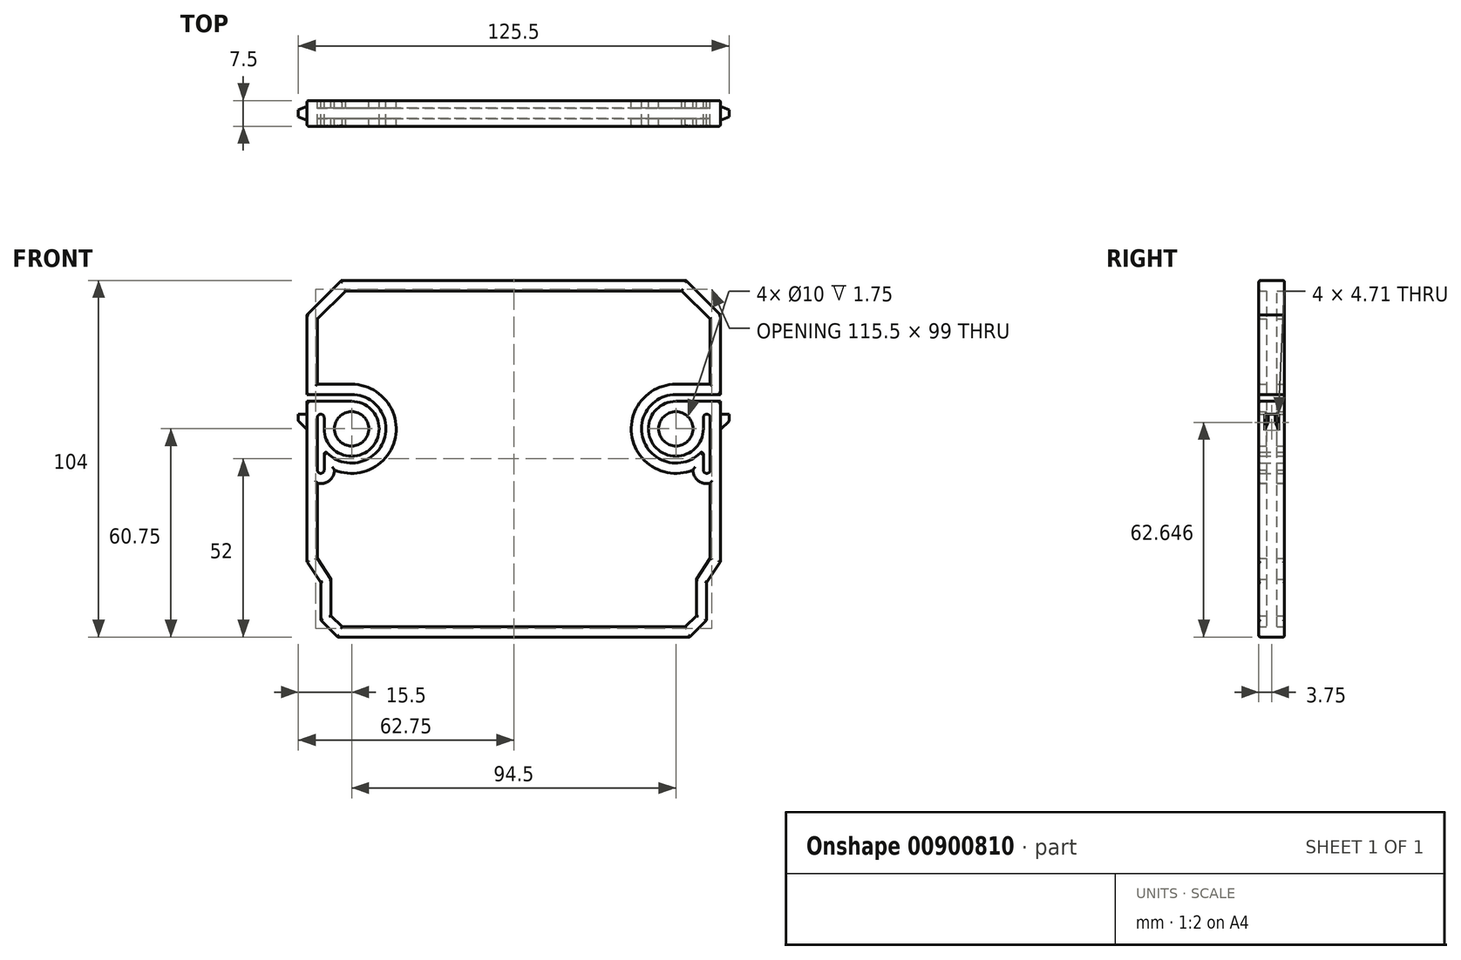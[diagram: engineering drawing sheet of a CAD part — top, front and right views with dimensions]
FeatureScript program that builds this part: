
annotation { "Feature Type Name" : "Feature", "Feature Type Description" : "" }
export const myFeature = defineFeature(function(context is Context, id is Id, definition is map)
    precondition{}
    {
        {
            var Q0;
            Q0=qCreatedBy(makeId("Front.planeOp"),FACE);
            var sketch = newSketch(context, id + "F0", { "sketchPlane" : qUnion([Q0])});
            skLineSegment(sketch, "E0.bottom", {"start": v(50.25, 52) * mm, "end": v(0, 52) * mm});
            skLineSegment(sketch, "E0.top", {"start": v(51.25, -52) * mm, "end": v(0, -52) * mm});
            skLineSegment(sketch, "E0.left", {"start": v(60.25, 42) * mm, "end": v(60.25, 18.75) * mm});
            skPoint(sketch, "E0.middle", {"position": v(0, 0) * mm});
            skLineSegment(sketch, "E1", {"start": v(50.25, 52) * mm, "end": v(60.25, 42) * mm});
            skPoint(sketch, "E2.orphan", {"position": v(60.25, 52) * mm});
            skLineSegment(sketch, "E3", {"start": v(60.25, -30) * mm, "end": v(56.25, -36) * mm});
            skLineSegment(sketch, "E4", {"start": v(56.25, -36) * mm, "end": v(56.25, -47) * mm});
            skLineSegment(sketch, "E5", {"start": v(56.25, -47) * mm, "end": v(51.25, -52) * mm});
            skPoint(sketch, "E6.orphan", {"position": v(60.25, -52) * mm});
            skLineSegment(sketch, "E7", {"start": v(60.25, 13) * mm, "end": v(62.75, 13) * mm});
            skLineSegment(sketch, "E8", {"start": v(62.75, 13) * mm, "end": v(62.75, 11) * mm});
            skLineSegment(sketch, "E9", {"start": v(62.75, 11) * mm, "end": v(60.25, 8.5) * mm});
            skLineSegment(sketch, "E10.trimOffspring", {"start": v(60.25, 8.5) * mm, "end": v(60.25, -30) * mm});
            skLineSegment(sketch, "E11.0", {"start": v(57.25, 42) * mm, "end": v(57.25, -30) * mm, "construction": true});
            skArc(sketch, "E12", {"start": v(47.25, 18.75) * mm, "mid": v(38.3, 4.28) * mm, "end": v(55.25, 2.75) * mm});
            skLineSegment(sketch, "E13", {"start": v(60.25, 18.75) * mm, "end": v(47.25, 18.75) * mm});
            skArc(sketch, "E14", {"start": v(47.25, 16.75) * mm, "mid": v(41.6, 3.1) * mm, "end": v(55.25, 8.75) * mm});
            skLineSegment(sketch, "E15", {"start": v(47.25, 16.75) * mm, "end": v(60.25, 16.75) * mm});
            skLineSegment(sketch, "E16.trimOffspring", {"start": v(60.25, 16.75) * mm, "end": v(60.25, 13) * mm});
            skLineSegment(sketch, "E17.0", {"start": v(55.25, 42) * mm, "end": v(55.25, -30) * mm, "construction": true});
            skArc(sketch, "E18", {"start": v(57.25, 12) * mm, "mid": v(56.25, 13) * mm, "end": v(55.25, 12) * mm});
            skArc(sketch, "E19", {"start": v(55.25, -3.25) * mm, "mid": v(56.25, -4.25) * mm, "end": v(57.25, -3.25) * mm});
            skLineSegment(sketch, "E20", {"start": v(55.25, 12) * mm, "end": v(55.25, 8.75) * mm});
            skLineSegment(sketch, "E21", {"start": v(57.25, 12) * mm, "end": v(57.25, -3.25) * mm});
            skLineSegment(sketch, "E22", {"start": v(55.25, -3.25) * mm, "end": v(55.25, 2.75) * mm});
            skLineSegment(sketch, "E23", {"start": v(0, 52) * mm, "end": v(0, -52) * mm});
            skLineSegment(sketch, "E24.trimOffspring", {"start": v(0, 18.75) * mm, "end": v(84.64, 18.75) * mm, "construction": true});
            skLineSegment(sketch, "E25.trimOffspring", {"start": v(0, 13) * mm, "end": v(110.3, 13) * mm, "construction": true});
            skLineSegment(sketch, "E26", {"start": v(0, 66.4) * mm, "end": v(0, -82.3) * mm, "construction": true});
            skLineSegment(sketch, "E27.MirrorCS", {"start": v(-55.25, 12) * mm, "end": v(-55.25, 8.75) * mm});
            skArc(sketch, "E28.MirrorCS", {"start": v(-55.25, -3.25) * mm, "mid": v(-56.25, -4.25) * mm, "end": v(-57.25, -3.25) * mm});
            skArc(sketch, "E29.MirrorCS", {"start": v(-57.25, 12) * mm, "mid": v(-56.25, 13) * mm, "end": v(-55.25, 12) * mm});
            skLineSegment(sketch, "E30.MirrorCS", {"start": v(-60.25, 13) * mm, "end": v(-62.75, 13) * mm});
            skLineSegment(sketch, "E31.MirrorCS", {"start": v(-60.25, 16.75) * mm, "end": v(-60.25, 13) * mm});
            skLineSegment(sketch, "E32.MirrorCS", {"start": v(-62.75, 13) * mm, "end": v(-62.75, 11) * mm});
            skLineSegment(sketch, "E33.MirrorCS", {"start": v(-56.25, -47) * mm, "end": v(-51.25, -52) * mm});
            skLineSegment(sketch, "E34.MirrorCS", {"start": v(-60.25, -30) * mm, "end": v(-56.25, -36) * mm});
            skLineSegment(sketch, "E35.MirrorCS", {"start": v(-55.25, -3.25) * mm, "end": v(-55.25, 2.75) * mm});
            skLineSegment(sketch, "E36.MirrorCS", {"start": v(-62.75, 11) * mm, "end": v(-60.25, 8.5) * mm});
            skLineSegment(sketch, "E37.MirrorCS", {"start": v(-57.25, 12) * mm, "end": v(-57.25, -3.25) * mm});
            skLineSegment(sketch, "E38.MirrorCS", {"start": v(-60.25, 18.75) * mm, "end": v(-47.25, 18.75) * mm});
            skLineSegment(sketch, "E39.MirrorCS", {"start": v(-57.25, 42) * mm, "end": v(-57.25, -30) * mm, "construction": true});
            skPoint(sketch, "E40.MirrorP", {"position": v(-60.25, 52) * mm});
            skLineSegment(sketch, "E41.MirrorCS", {"start": v(-51.25, -52) * mm, "end": v(0, -52) * mm});
            skLineSegment(sketch, "E42.MirrorCS", {"start": v(-50.25, 52) * mm, "end": v(0, 52) * mm});
            skArc(sketch, "E43.MirrorCS", {"start": v(-47.25, 18.75) * mm, "mid": v(-38.3, 4.28) * mm, "end": v(-55.25, 2.75) * mm});
            skLineSegment(sketch, "E44.MirrorCS", {"start": v(-50.25, 52) * mm, "end": v(-60.25, 42) * mm});
            skLineSegment(sketch, "E45.MirrorCS", {"start": v(-55.25, 42) * mm, "end": v(-55.25, -30) * mm, "construction": true});
            skLineSegment(sketch, "E46.MirrorCS", {"start": v(-47.25, 16.75) * mm, "end": v(-60.25, 16.75) * mm});
            skPoint(sketch, "E47.MirrorP", {"position": v(-60.25, -52) * mm});
            skLineSegment(sketch, "E48.MirrorCS", {"start": v(-60.25, 42) * mm, "end": v(-60.25, 18.75) * mm});
            skLineSegment(sketch, "E49.MirrorCS", {"start": v(0, 13) * mm, "end": v(-110.3, 13) * mm, "construction": true});
            skLineSegment(sketch, "E50.MirrorCS", {"start": v(-60.25, 8.5) * mm, "end": v(-60.25, -30) * mm});
            skArc(sketch, "E51.MirrorCS", {"start": v(-47.25, 16.75) * mm, "mid": v(-41.6, 3.1) * mm, "end": v(-55.25, 8.75) * mm});
            skLineSegment(sketch, "E52.MirrorCS", {"start": v(0, 18.75) * mm, "end": v(-84.64, 18.75) * mm, "construction": true});
            skLineSegment(sketch, "E53.MirrorCS", {"start": v(-56.25, -36) * mm, "end": v(-56.25, -47) * mm});
            skSolve(sketch);
        }
        {
            var Q0;
            Q0 = qSketchRegion(id + "F0", true);
            extrude(context, id + "F1", {"entities" : qUnion([Q0]), "endBound" : BoundingType.SYMMETRIC, "depth" : 3 * mm, "offsetDistance" : 25 * mm});
        }
        {
            var Q0;
            Q0=qCreatedBy(makeId("Front.planeOp"),FACE);
            var sketch = newSketch(context, id + "F2", { "sketchPlane" : qUnion([Q0])});
            skLineSegment(sketch, "E54.0.0", {"start": v(0, 52) * mm, "end": v(-50.25, 52) * mm});
            skLineSegment(sketch, "E54.0.1", {"start": v(-50.25, 52) * mm, "end": v(-60.25, 42) * mm});
            skLineSegment(sketch, "E54.0.2", {"start": v(-60.25, 42) * mm, "end": v(-60.25, 18.75) * mm});
            skLineSegment(sketch, "E54.0.3", {"start": v(-60.25, 18.75) * mm, "end": v(-47.25, 18.75) * mm});
            skArc(sketch, "E54.0.4", {"start": v(-47.25, 18.75) * mm, "mid": v(-38.3, 4.28) * mm, "end": v(-55.25, 2.75) * mm});
            skLineSegment(sketch, "E54.0.5", {"start": v(-55.25, 2.75) * mm, "end": v(-55.25, -3.25) * mm});
            skArc(sketch, "E54.0.6", {"start": v(-55.25, -3.25) * mm, "mid": v(-56.25, -4.25) * mm, "end": v(-57.25, -3.25) * mm});
            skArc(sketch, "E54.0.8", {"start": v(-57.25, 12) * mm, "mid": v(-56.25, 13) * mm, "end": v(-55.25, 12) * mm});
            skLineSegment(sketch, "E54.0.9", {"start": v(-55.25, 12) * mm, "end": v(-55.25, 8.75) * mm});
            skArc(sketch, "E54.0.10", {"start": v(-55.25, 8.75) * mm, "mid": v(-41.6, 3.1) * mm, "end": v(-47.25, 16.75) * mm});
            skLineSegment(sketch, "E54.0.11", {"start": v(-47.25, 16.75) * mm, "end": v(-60.25, 16.75) * mm});
            skLineSegment(sketch, "E54.0.12", {"start": v(-60.25, 16.75) * mm, "end": v(-60.25, 13) * mm});
            skLineSegment(sketch, "E54.0.13", {"start": v(-60.25, 13) * mm, "end": v(-62.75, 13) * mm});
            skLineSegment(sketch, "E54.0.14", {"start": v(-62.75, 13) * mm, "end": v(-62.75, 11) * mm});
            skLineSegment(sketch, "E54.0.15", {"start": v(-62.75, 11) * mm, "end": v(-60.25, 8.5) * mm});
            skLineSegment(sketch, "E54.0.16", {"start": v(-60.25, 8.5) * mm, "end": v(-60.25, -30) * mm});
            skLineSegment(sketch, "E54.0.17", {"start": v(-60.25, -30) * mm, "end": v(-56.25, -36) * mm});
            skLineSegment(sketch, "E54.0.18", {"start": v(-56.25, -36) * mm, "end": v(-56.25, -47) * mm});
            skLineSegment(sketch, "E54.0.19", {"start": v(-56.25, -47) * mm, "end": v(-51.25, -52) * mm});
            skLineSegment(sketch, "E54.0.20", {"start": v(-51.25, -52) * mm, "end": v(0, -52) * mm});
            skLineSegment(sketch, "E54.0.21", {"start": v(0, -49) * mm, "end": v(0, 49) * mm, "construction": true});
            skLineSegment(sketch, "E55.0.0", {"start": v(0, -52) * mm, "end": v(51.25, -52) * mm});
            skLineSegment(sketch, "E55.0.1", {"start": v(51.25, -52) * mm, "end": v(56.25, -47) * mm});
            skLineSegment(sketch, "E55.0.2", {"start": v(56.25, -47) * mm, "end": v(56.25, -36) * mm});
            skLineSegment(sketch, "E55.0.3", {"start": v(56.25, -36) * mm, "end": v(60.25, -30) * mm});
            skLineSegment(sketch, "E55.0.4", {"start": v(60.25, -30) * mm, "end": v(60.25, 8.5) * mm});
            skLineSegment(sketch, "E55.0.5", {"start": v(60.25, 8.5) * mm, "end": v(62.75, 11) * mm});
            skLineSegment(sketch, "E55.0.6", {"start": v(62.75, 11) * mm, "end": v(62.75, 13) * mm});
            skLineSegment(sketch, "E55.0.7", {"start": v(62.75, 13) * mm, "end": v(60.25, 13) * mm});
            skLineSegment(sketch, "E55.0.8", {"start": v(60.25, 13) * mm, "end": v(60.25, 16.75) * mm});
            skLineSegment(sketch, "E55.0.9", {"start": v(60.25, 16.75) * mm, "end": v(47.25, 16.75) * mm});
            skArc(sketch, "E55.0.10", {"start": v(47.25, 16.75) * mm, "mid": v(41.6, 3.1) * mm, "end": v(55.25, 8.75) * mm});
            skLineSegment(sketch, "E55.0.11", {"start": v(55.25, 8.75) * mm, "end": v(55.25, 12) * mm});
            skArc(sketch, "E55.0.12", {"start": v(55.25, 12) * mm, "mid": v(56.25, 13) * mm, "end": v(57.25, 12) * mm});
            skArc(sketch, "E55.0.14", {"start": v(57.25, -3.25) * mm, "mid": v(56.25, -4.25) * mm, "end": v(55.25, -3.25) * mm});
            skLineSegment(sketch, "E55.0.15", {"start": v(55.25, -3.25) * mm, "end": v(55.25, 2.75) * mm});
            skArc(sketch, "E55.0.16", {"start": v(55.25, 2.75) * mm, "mid": v(38.3, 4.28) * mm, "end": v(47.25, 18.75) * mm});
            skLineSegment(sketch, "E55.0.17", {"start": v(47.25, 18.75) * mm, "end": v(60.25, 18.75) * mm});
            skLineSegment(sketch, "E55.0.18", {"start": v(60.25, 18.75) * mm, "end": v(60.25, 42) * mm});
            skLineSegment(sketch, "E55.0.19", {"start": v(60.25, 42) * mm, "end": v(50.25, 52) * mm});
            skLineSegment(sketch, "E55.0.20", {"start": v(50.25, 52) * mm, "end": v(0, 52) * mm});
            skLineSegment(sketch, "E55.0.21", {"start": v(0, 49) * mm, "end": v(0, -49) * mm});
            skArc(sketch, "E56.0", {"start": v(-47.25, 21.75) * mm, "mid": v(-34.5, 6.2) * mm, "end": v(-52.25, -3.25) * mm});
            skLineSegment(sketch, "E56.1", {"start": v(-57.25, 21.75) * mm, "end": v(-47.25, 21.75) * mm});
            skLineSegment(sketch, "E56.2", {"start": v(-57.25, 40.76) * mm, "end": v(-57.25, 21.75) * mm});
            skLineSegment(sketch, "E56.3", {"start": v(-49, 49) * mm, "end": v(-57.25, 40.76) * mm});
            skLineSegment(sketch, "E56.4", {"start": v(0, 49) * mm, "end": v(-49, 49) * mm});
            skLineSegment(sketch, "E56.5", {"start": v(49, 49) * mm, "end": v(0, 49) * mm});
            skLineSegment(sketch, "E56.7", {"start": v(47.25, 21.75) * mm, "end": v(57.25, 21.75) * mm});
            skLineSegment(sketch, "E56.8", {"start": v(57.25, 21.75) * mm, "end": v(57.25, 40.76) * mm});
            skLineSegment(sketch, "E56.9", {"start": v(57.25, 40.76) * mm, "end": v(49, 49) * mm});
            skArc(sketch, "E57.0", {"start": v(57.25, -7.12) * mm, "mid": v(53.8, -6.41) * mm, "end": v(52.25, -3.25) * mm});
            skArc(sketch, "E58.trimOffspring", {"start": v(52.25, -3.25) * mm, "mid": v(34.5, 6.2) * mm, "end": v(47.25, 21.75) * mm});
            skCircle(sketch, "E59", {"center": v(47.25, 8.75) * mm, "radius": 5 * mm});
            skArc(sketch, "E60.0", {"start": v(-52.25, -3.25) * mm, "mid": v(-53.8, -6.41) * mm, "end": v(-57.25, -7.12) * mm});
            skLineSegment(sketch, "E61.0", {"start": v(57.25, -29.1) * mm, "end": v(57.25, -7.12) * mm});
            skLineSegment(sketch, "E61.1", {"start": v(53.25, -35.1) * mm, "end": v(57.25, -29.1) * mm});
            skLineSegment(sketch, "E61.2", {"start": v(53.25, -45.76) * mm, "end": v(53.25, -35.1) * mm});
            skLineSegment(sketch, "E61.3", {"start": v(50, -49) * mm, "end": v(53.25, -45.76) * mm});
            skLineSegment(sketch, "E61.4", {"start": v(0, -49) * mm, "end": v(50, -49) * mm});
            skLineSegment(sketch, "E61.5", {"start": v(-50, -49) * mm, "end": v(0, -49) * mm});
            skLineSegment(sketch, "E61.7", {"start": v(-57.25, -29.1) * mm, "end": v(-53.25, -35.1) * mm});
            skLineSegment(sketch, "E61.8", {"start": v(-53.25, -35.1) * mm, "end": v(-53.25, -45.76) * mm});
            skLineSegment(sketch, "E61.9", {"start": v(-53.25, -45.76) * mm, "end": v(-50, -49) * mm});
            skLineSegment(sketch, "E62.trimOffspring", {"start": v(-57.25, -7.12) * mm, "end": v(-57.25, -29.1) * mm});
            skLineSegment(sketch, "E63", {"start": v(57.25, 12) * mm, "end": v(57.25, -3.25) * mm});
            skLineSegment(sketch, "E64", {"start": v(-57.25, 12) * mm, "end": v(-57.25, -3.25) * mm});
            skCircle(sketch, "E65", {"center": v(-47.25, 8.75) * mm, "radius": 5 * mm});
            skSolve(sketch);
        }
        {
            var Q0;
            Q0 = qSketchRegion(id + "F2", true);
            extrude(context, id + "F3", {"entities" : qUnion([Q0]), "endBound" : BoundingType.SYMMETRIC, "depth" : 7.5 * mm, "offsetDistance" : 25 * mm});
        }
        {
            var Q0;
            Q0=makeQuery(id+"F1.opExtrude","SWEPT_BODY",BODY,{"disambiguationData":[OSD([sQuery(id+"F0.wireOp",EDGE,"E0.bottom"),sQuery(id+"F0.wireOp",EDGE,"E0.top"),sQuery(id+"F0.wireOp",EDGE,"E0.left"),sQuery(id+"F0.wireOp",EDGE,"E1"),sQuery(id+"F0.wireOp",EDGE,"E3"),sQuery(id+"F0.wireOp",EDGE,"E4"),sQuery(id+"F0.wireOp",EDGE,"E5"),sQuery(id+"F0.wireOp",EDGE,"E7"),sQuery(id+"F0.wireOp",EDGE,"E8"),sQuery(id+"F0.wireOp",EDGE,"E9"),sQuery(id+"F0.wireOp",EDGE,"E10.trimOffspring"),sQuery(id+"F0.wireOp",EDGE,"E12"),sQuery(id+"F0.wireOp",EDGE,"E13"),sQuery(id+"F0.wireOp",EDGE,"E14"),sQuery(id+"F0.wireOp",EDGE,"E15"),sQuery(id+"F0.wireOp",EDGE,"E16.trimOffspring"),sQuery(id+"F0.wireOp",EDGE,"E18"),sQuery(id+"F0.wireOp",EDGE,"E19"),sQuery(id+"F0.wireOp",EDGE,"E20"),sQuery(id+"F0.wireOp",EDGE,"E21"),sQuery(id+"F0.wireOp",EDGE,"E22"),sQuery(id+"F0.wireOp",EDGE,"E27.MirrorCS"),sQuery(id+"F0.wireOp",EDGE,"E28.MirrorCS"),sQuery(id+"F0.wireOp",EDGE,"E29.MirrorCS"),sQuery(id+"F0.wireOp",EDGE,"E30.MirrorCS"),sQuery(id+"F0.wireOp",EDGE,"E31.MirrorCS"),sQuery(id+"F0.wireOp",EDGE,"E32.MirrorCS"),sQuery(id+"F0.wireOp",EDGE,"E33.MirrorCS"),sQuery(id+"F0.wireOp",EDGE,"E34.MirrorCS"),sQuery(id+"F0.wireOp",EDGE,"E35.MirrorCS"),sQuery(id+"F0.wireOp",EDGE,"E36.MirrorCS"),sQuery(id+"F0.wireOp",EDGE,"E37.MirrorCS"),sQuery(id+"F0.wireOp",EDGE,"E38.MirrorCS"),sQuery(id+"F0.wireOp",EDGE,"E41.MirrorCS"),sQuery(id+"F0.wireOp",EDGE,"E42.MirrorCS"),sQuery(id+"F0.wireOp",EDGE,"E43.MirrorCS"),sQuery(id+"F0.wireOp",EDGE,"E44.MirrorCS"),sQuery(id+"F0.wireOp",EDGE,"E46.MirrorCS"),sQuery(id+"F0.wireOp",EDGE,"E48.MirrorCS"),sQuery(id+"F0.wireOp",EDGE,"E50.MirrorCS"),sQuery(id+"F0.wireOp",EDGE,"E51.MirrorCS"),sQuery(id+"F0.wireOp",EDGE,"E53.MirrorCS")])]});
            var Q1;
            Q1=makeQuery(id+"F3.opExtrude","SWEPT_BODY",BODY,{"disambiguationData":[OSD([sQuery(id+"F2.wireOp",EDGE,"E54.0.0"),sQuery(id+"F2.wireOp",EDGE,"E54.0.1"),sQuery(id+"F2.wireOp",EDGE,"E54.0.2"),sQuery(id+"F2.wireOp",EDGE,"E54.0.3"),sQuery(id+"F2.wireOp",EDGE,"E54.0.4"),sQuery(id+"F2.wireOp",EDGE,"E54.0.5"),sQuery(id+"F2.wireOp",EDGE,"E54.0.6"),sQuery(id+"F2.wireOp",EDGE,"E54.0.8"),sQuery(id+"F2.wireOp",EDGE,"E54.0.9"),sQuery(id+"F2.wireOp",EDGE,"E54.0.10"),sQuery(id+"F2.wireOp",EDGE,"E54.0.11"),sQuery(id+"F2.wireOp",EDGE,"E54.0.12"),sQuery(id+"F2.wireOp",EDGE,"E54.0.13"),sQuery(id+"F2.wireOp",EDGE,"E54.0.14"),sQuery(id+"F2.wireOp",EDGE,"E54.0.15"),sQuery(id+"F2.wireOp",EDGE,"E54.0.16"),sQuery(id+"F2.wireOp",EDGE,"E54.0.17"),sQuery(id+"F2.wireOp",EDGE,"E54.0.18"),sQuery(id+"F2.wireOp",EDGE,"E54.0.19"),sQuery(id+"F2.wireOp",EDGE,"E54.0.20"),sQuery(id+"F2.wireOp",EDGE,"E55.0.0"),sQuery(id+"F2.wireOp",EDGE,"E55.0.1"),sQuery(id+"F2.wireOp",EDGE,"E55.0.2"),sQuery(id+"F2.wireOp",EDGE,"E55.0.3"),sQuery(id+"F2.wireOp",EDGE,"E55.0.4"),sQuery(id+"F2.wireOp",EDGE,"E55.0.5"),sQuery(id+"F2.wireOp",EDGE,"E55.0.6"),sQuery(id+"F2.wireOp",EDGE,"E55.0.7"),sQuery(id+"F2.wireOp",EDGE,"E55.0.8"),sQuery(id+"F2.wireOp",EDGE,"E55.0.9"),sQuery(id+"F2.wireOp",EDGE,"E55.0.10"),sQuery(id+"F2.wireOp",EDGE,"E55.0.11"),sQuery(id+"F2.wireOp",EDGE,"E55.0.12"),sQuery(id+"F2.wireOp",EDGE,"E55.0.14"),sQuery(id+"F2.wireOp",EDGE,"E55.0.15"),sQuery(id+"F2.wireOp",EDGE,"E55.0.16"),sQuery(id+"F2.wireOp",EDGE,"E55.0.17"),sQuery(id+"F2.wireOp",EDGE,"E55.0.18"),sQuery(id+"F2.wireOp",EDGE,"E55.0.19"),sQuery(id+"F2.wireOp",EDGE,"E55.0.20"),sQuery(id+"F2.wireOp",EDGE,"E56.0"),sQuery(id+"F2.wireOp",EDGE,"E56.1"),sQuery(id+"F2.wireOp",EDGE,"E56.2"),sQuery(id+"F2.wireOp",EDGE,"E56.3"),sQuery(id+"F2.wireOp",EDGE,"E56.4"),sQuery(id+"F2.wireOp",EDGE,"E56.5"),sQuery(id+"F2.wireOp",EDGE,"E56.7"),sQuery(id+"F2.wireOp",EDGE,"E56.8"),sQuery(id+"F2.wireOp",EDGE,"E56.9"),sQuery(id+"F2.wireOp",EDGE,"E57.0"),sQuery(id+"F2.wireOp",EDGE,"E58.trimOffspring"),sQuery(id+"F2.wireOp",EDGE,"E59"),sQuery(id+"F2.wireOp",EDGE,"E60.0"),sQuery(id+"F2.wireOp",EDGE,"E61.0"),sQuery(id+"F2.wireOp",EDGE,"E61.1"),sQuery(id+"F2.wireOp",EDGE,"E61.2"),sQuery(id+"F2.wireOp",EDGE,"E61.3"),sQuery(id+"F2.wireOp",EDGE,"E61.4"),sQuery(id+"F2.wireOp",EDGE,"E61.5"),sQuery(id+"F2.wireOp",EDGE,"E61.7"),sQuery(id+"F2.wireOp",EDGE,"E61.8"),sQuery(id+"F2.wireOp",EDGE,"E61.9"),sQuery(id+"F2.wireOp",EDGE,"E62.trimOffspring"),sQuery(id+"F2.wireOp",EDGE,"E63"),sQuery(id+"F2.wireOp",EDGE,"E64"),sQuery(id+"F2.wireOp",EDGE,"E65")])]});
            booleanBodies(context, id + "F4", {"operationType" : BooleanOperationType.UNION, "tools" : qUnion([Q0, Q1])});
        }
        {
            var Q0;
            Q0=qCreatedBy(makeId("Top.planeOp"),FACE);
            var sketch = newSketch(context, id + "F5", { "sketchPlane" : qUnion([Q0])});
            skLineSegment(sketch, "E66.0.0", {"start": v(-60.25, -3.75) * mm, "end": v(-60.25, 3.75) * mm});
            skLineSegment(sketch, "E66.0.1", {"start": v(-60.25, 3.75) * mm, "end": v(-62.75, 3.75) * mm});
            skLineSegment(sketch, "E66.0.2", {"start": v(-62.75, 3.75) * mm, "end": v(-62.75, -3.75) * mm});
            skLineSegment(sketch, "E66.0.3", {"start": v(-62.75, -3.75) * mm, "end": v(-60.25, -3.75) * mm});
            skLineSegment(sketch, "E67.0.0", {"start": v(62.75, -3.75) * mm, "end": v(62.75, 3.75) * mm});
            skLineSegment(sketch, "E67.0.1", {"start": v(62.75, 3.75) * mm, "end": v(60.25, 3.75) * mm});
            skLineSegment(sketch, "E67.0.2", {"start": v(60.25, 3.75) * mm, "end": v(60.25, -3.75) * mm});
            skLineSegment(sketch, "E67.0.3", {"start": v(60.25, -3.75) * mm, "end": v(62.75, -3.75) * mm});
            skLineSegment(sketch, "E68", {"start": v(-60.25, 3.75) * mm, "end": v(-60.25, 2) * mm});
            skLineSegment(sketch, "E69", {"start": v(-62.75, 3.75) * mm, "end": v(-62.75, 1) * mm});
            skLineSegment(sketch, "E70", {"start": v(-60.25, 2) * mm, "end": v(-62.75, 1) * mm});
            skLineSegment(sketch, "E71", {"start": v(-62.75, 1) * mm, "end": v(-62.75, -1) * mm});
            skLineSegment(sketch, "E72", {"start": v(-60.25, -3.75) * mm, "end": v(-60.25, -2) * mm});
            skLineSegment(sketch, "E73", {"start": v(-60.25, -2) * mm, "end": v(-62.75, -1) * mm});
            skLineSegment(sketch, "E74", {"start": v(60.25, 3.75) * mm, "end": v(60.25, 2) * mm});
            skLineSegment(sketch, "E75", {"start": v(62.75, 3.75) * mm, "end": v(62.75, 1) * mm});
            skLineSegment(sketch, "E76", {"start": v(62.75, 1) * mm, "end": v(60.25, 2) * mm});
            skLineSegment(sketch, "E77", {"start": v(60.25, -3.75) * mm, "end": v(60.25, -2) * mm});
            skLineSegment(sketch, "E78", {"start": v(62.75, 1) * mm, "end": v(62.75, -1) * mm});
            skLineSegment(sketch, "E79", {"start": v(62.75, -1) * mm, "end": v(60.25, -2) * mm});
            skSolve(sketch);
        }
        {
            var Q0;
            {var subQ0=sQuery(id+"F5.wireOp",EDGE,"E66.0.1");Q0=makeQuery(id+"F5.imprint","IMPRINT",FACE,{"disambiguationData":[TD([[makeQuery(id+"F5.imprint","IMPRINT",EDGE,{"derivedFrom":subQ0}),1.0]])]});}
            var Q1;
            {var subQ2=sQuery(id+"F5.wireOp",EDGE,"E66.0.3");Q1=makeQuery(id+"F5.imprint","IMPRINT",FACE,{"disambiguationData":[TD([[makeQuery(id+"F5.imprint","IMPRINT",EDGE,{"derivedFrom":subQ2}),1.0]])]});}
            var Q2;
            {var subQ2=sQuery(id+"F5.wireOp",EDGE,"E67.0.1");Q2=makeQuery(id+"F5.imprint","IMPRINT",FACE,{"disambiguationData":[TD([[makeQuery(id+"F5.imprint","IMPRINT",EDGE,{"derivedFrom":subQ2}),1.0]])]});}
            var Q3;
            {var subQ0=sQuery(id+"F5.wireOp",EDGE,"E67.0.3");Q3=makeQuery(id+"F5.imprint","IMPRINT",FACE,{"disambiguationData":[TD([[makeQuery(id+"F5.imprint","IMPRINT",EDGE,{"derivedFrom":subQ0}),1.0]])]});}
            extrude(context, id + "F6", {"entities" : qUnion([Q0, Q1, Q2, Q3]), "operationType" : NewBodyOperationType.REMOVE, "endBound" : BoundingType.THROUGH_ALL, "depth" : 25 * mm, "offsetDistance" : 25 * mm});
        }
        {
            var Q0;
            Q0=makeQuery(id+"F3.opExtrude","CAP_FACE",FACE,{"disambiguationData":[OSD([sQuery(id+"F2.wireOp",EDGE,"E54.0.0"),sQuery(id+"F2.wireOp",EDGE,"E54.0.1"),sQuery(id+"F2.wireOp",EDGE,"E54.0.2"),sQuery(id+"F2.wireOp",EDGE,"E54.0.3"),sQuery(id+"F2.wireOp",EDGE,"E54.0.4"),sQuery(id+"F2.wireOp",EDGE,"E54.0.5"),sQuery(id+"F2.wireOp",EDGE,"E54.0.6"),sQuery(id+"F2.wireOp",EDGE,"E54.0.8"),sQuery(id+"F2.wireOp",EDGE,"E54.0.9"),sQuery(id+"F2.wireOp",EDGE,"E54.0.10"),sQuery(id+"F2.wireOp",EDGE,"E54.0.11"),sQuery(id+"F2.wireOp",EDGE,"E54.0.12"),sQuery(id+"F2.wireOp",EDGE,"E54.0.13"),sQuery(id+"F2.wireOp",EDGE,"E54.0.14"),sQuery(id+"F2.wireOp",EDGE,"E54.0.15"),sQuery(id+"F2.wireOp",EDGE,"E54.0.16"),sQuery(id+"F2.wireOp",EDGE,"E54.0.17"),sQuery(id+"F2.wireOp",EDGE,"E54.0.18"),sQuery(id+"F2.wireOp",EDGE,"E54.0.19"),sQuery(id+"F2.wireOp",EDGE,"E54.0.20"),sQuery(id+"F2.wireOp",EDGE,"E55.0.0"),sQuery(id+"F2.wireOp",EDGE,"E55.0.1"),sQuery(id+"F2.wireOp",EDGE,"E55.0.2"),sQuery(id+"F2.wireOp",EDGE,"E55.0.3"),sQuery(id+"F2.wireOp",EDGE,"E55.0.4"),sQuery(id+"F2.wireOp",EDGE,"E55.0.5"),sQuery(id+"F2.wireOp",EDGE,"E55.0.6"),sQuery(id+"F2.wireOp",EDGE,"E55.0.7"),sQuery(id+"F2.wireOp",EDGE,"E55.0.8"),sQuery(id+"F2.wireOp",EDGE,"E55.0.9"),sQuery(id+"F2.wireOp",EDGE,"E55.0.10"),sQuery(id+"F2.wireOp",EDGE,"E55.0.11"),sQuery(id+"F2.wireOp",EDGE,"E55.0.12"),sQuery(id+"F2.wireOp",EDGE,"E55.0.14"),sQuery(id+"F2.wireOp",EDGE,"E55.0.15"),sQuery(id+"F2.wireOp",EDGE,"E55.0.16"),sQuery(id+"F2.wireOp",EDGE,"E55.0.17"),sQuery(id+"F2.wireOp",EDGE,"E55.0.18"),sQuery(id+"F2.wireOp",EDGE,"E55.0.19"),sQuery(id+"F2.wireOp",EDGE,"E55.0.20"),sQuery(id+"F2.wireOp",EDGE,"E56.0"),sQuery(id+"F2.wireOp",EDGE,"E56.1"),sQuery(id+"F2.wireOp",EDGE,"E56.2"),sQuery(id+"F2.wireOp",EDGE,"E56.3"),sQuery(id+"F2.wireOp",EDGE,"E56.4"),sQuery(id+"F2.wireOp",EDGE,"E56.5"),sQuery(id+"F2.wireOp",EDGE,"E56.7"),sQuery(id+"F2.wireOp",EDGE,"E56.8"),sQuery(id+"F2.wireOp",EDGE,"E56.9"),sQuery(id+"F2.wireOp",EDGE,"E57.0"),sQuery(id+"F2.wireOp",EDGE,"E58.trimOffspring"),sQuery(id+"F2.wireOp",EDGE,"E59"),sQuery(id+"F2.wireOp",EDGE,"E60.0"),sQuery(id+"F2.wireOp",EDGE,"E61.0"),sQuery(id+"F2.wireOp",EDGE,"E61.1"),sQuery(id+"F2.wireOp",EDGE,"E61.2"),sQuery(id+"F2.wireOp",EDGE,"E61.3"),sQuery(id+"F2.wireOp",EDGE,"E61.4"),sQuery(id+"F2.wireOp",EDGE,"E61.5"),sQuery(id+"F2.wireOp",EDGE,"E61.7"),sQuery(id+"F2.wireOp",EDGE,"E61.8"),sQuery(id+"F2.wireOp",EDGE,"E61.9"),sQuery(id+"F2.wireOp",EDGE,"E62.trimOffspring"),sQuery(id+"F2.wireOp",EDGE,"E63"),sQuery(id+"F2.wireOp",EDGE,"E64"),sQuery(id+"F2.wireOp",EDGE,"E65")])],"isStart":false});
            var Q1;
            Q1=makeQuery(id+"F3.opExtrude","CAP_FACE",FACE,{"disambiguationData":[OSD([sQuery(id+"F2.wireOp",EDGE,"E54.0.0"),sQuery(id+"F2.wireOp",EDGE,"E54.0.1"),sQuery(id+"F2.wireOp",EDGE,"E54.0.2"),sQuery(id+"F2.wireOp",EDGE,"E54.0.3"),sQuery(id+"F2.wireOp",EDGE,"E54.0.4"),sQuery(id+"F2.wireOp",EDGE,"E54.0.5"),sQuery(id+"F2.wireOp",EDGE,"E54.0.6"),sQuery(id+"F2.wireOp",EDGE,"E54.0.8"),sQuery(id+"F2.wireOp",EDGE,"E54.0.9"),sQuery(id+"F2.wireOp",EDGE,"E54.0.10"),sQuery(id+"F2.wireOp",EDGE,"E54.0.11"),sQuery(id+"F2.wireOp",EDGE,"E54.0.12"),sQuery(id+"F2.wireOp",EDGE,"E54.0.13"),sQuery(id+"F2.wireOp",EDGE,"E54.0.14"),sQuery(id+"F2.wireOp",EDGE,"E54.0.15"),sQuery(id+"F2.wireOp",EDGE,"E54.0.16"),sQuery(id+"F2.wireOp",EDGE,"E54.0.17"),sQuery(id+"F2.wireOp",EDGE,"E54.0.18"),sQuery(id+"F2.wireOp",EDGE,"E54.0.19"),sQuery(id+"F2.wireOp",EDGE,"E54.0.20"),sQuery(id+"F2.wireOp",EDGE,"E55.0.0"),sQuery(id+"F2.wireOp",EDGE,"E55.0.1"),sQuery(id+"F2.wireOp",EDGE,"E55.0.2"),sQuery(id+"F2.wireOp",EDGE,"E55.0.3"),sQuery(id+"F2.wireOp",EDGE,"E55.0.4"),sQuery(id+"F2.wireOp",EDGE,"E55.0.5"),sQuery(id+"F2.wireOp",EDGE,"E55.0.6"),sQuery(id+"F2.wireOp",EDGE,"E55.0.7"),sQuery(id+"F2.wireOp",EDGE,"E55.0.8"),sQuery(id+"F2.wireOp",EDGE,"E55.0.9"),sQuery(id+"F2.wireOp",EDGE,"E55.0.10"),sQuery(id+"F2.wireOp",EDGE,"E55.0.11"),sQuery(id+"F2.wireOp",EDGE,"E55.0.12"),sQuery(id+"F2.wireOp",EDGE,"E55.0.14"),sQuery(id+"F2.wireOp",EDGE,"E55.0.15"),sQuery(id+"F2.wireOp",EDGE,"E55.0.16"),sQuery(id+"F2.wireOp",EDGE,"E55.0.17"),sQuery(id+"F2.wireOp",EDGE,"E55.0.18"),sQuery(id+"F2.wireOp",EDGE,"E55.0.19"),sQuery(id+"F2.wireOp",EDGE,"E55.0.20"),sQuery(id+"F2.wireOp",EDGE,"E56.0"),sQuery(id+"F2.wireOp",EDGE,"E56.1"),sQuery(id+"F2.wireOp",EDGE,"E56.2"),sQuery(id+"F2.wireOp",EDGE,"E56.3"),sQuery(id+"F2.wireOp",EDGE,"E56.4"),sQuery(id+"F2.wireOp",EDGE,"E56.5"),sQuery(id+"F2.wireOp",EDGE,"E56.7"),sQuery(id+"F2.wireOp",EDGE,"E56.8"),sQuery(id+"F2.wireOp",EDGE,"E56.9"),sQuery(id+"F2.wireOp",EDGE,"E57.0"),sQuery(id+"F2.wireOp",EDGE,"E58.trimOffspring"),sQuery(id+"F2.wireOp",EDGE,"E59"),sQuery(id+"F2.wireOp",EDGE,"E60.0"),sQuery(id+"F2.wireOp",EDGE,"E61.0"),sQuery(id+"F2.wireOp",EDGE,"E61.1"),sQuery(id+"F2.wireOp",EDGE,"E61.2"),sQuery(id+"F2.wireOp",EDGE,"E61.3"),sQuery(id+"F2.wireOp",EDGE,"E61.4"),sQuery(id+"F2.wireOp",EDGE,"E61.5"),sQuery(id+"F2.wireOp",EDGE,"E61.7"),sQuery(id+"F2.wireOp",EDGE,"E61.8"),sQuery(id+"F2.wireOp",EDGE,"E61.9"),sQuery(id+"F2.wireOp",EDGE,"E62.trimOffspring"),sQuery(id+"F2.wireOp",EDGE,"E63"),sQuery(id+"F2.wireOp",EDGE,"E64"),sQuery(id+"F2.wireOp",EDGE,"E65")])],"isStart":true});
            fillet(context, id + "F7", {"entities" : qUnion([Q0, Q1]), "radius" : 0.5 * mm, "tangentPropagation" : true, "allowEdgeOverflow" : false});
        }
        {
            var Q0;
            Q0=makeQuery(id+"F4.opBoolean","MERGE",EDGE,{"derivedFrom":[makeQuery(id+"F1.opExtrude","SWEPT_EDGE",EDGE,{"disambiguationData":[OSD([sQuery(id+"F0.wireOp",EDGE,"E44.MirrorCS"),sQuery(id+"F0.wireOp",EDGE,"E48.MirrorCS")])]}),makeQuery(id+"F3.opExtrude","SWEPT_EDGE",EDGE,{"disambiguationData":[OSD([sQuery(id+"F2.wireOp",EDGE,"E54.0.1"),sQuery(id+"F2.wireOp",EDGE,"E54.0.2")])]})]});
            var Q1;
            Q1=makeQuery(id+"F4.opBoolean","MERGE",EDGE,{"derivedFrom":[makeQuery(id+"F1.opExtrude","SWEPT_EDGE",EDGE,{"disambiguationData":[OSD([sQuery(id+"F0.wireOp",EDGE,"E42.MirrorCS"),sQuery(id+"F0.wireOp",EDGE,"E44.MirrorCS")])]}),makeQuery(id+"F3.opExtrude","SWEPT_EDGE",EDGE,{"disambiguationData":[OSD([sQuery(id+"F2.wireOp",EDGE,"E54.0.0"),sQuery(id+"F2.wireOp",EDGE,"E54.0.1")])]})]});
            var Q2;
            Q2=makeQuery(id+"F4.opBoolean","MERGE",EDGE,{"derivedFrom":[makeQuery(id+"F1.opExtrude","SWEPT_EDGE",EDGE,{"disambiguationData":[OSD([sQuery(id+"F0.wireOp",EDGE,"E38.MirrorCS"),sQuery(id+"F0.wireOp",EDGE,"E48.MirrorCS")])]}),makeQuery(id+"F3.opExtrude","SWEPT_EDGE",EDGE,{"disambiguationData":[OSD([sQuery(id+"F2.wireOp",EDGE,"E54.0.2"),sQuery(id+"F2.wireOp",EDGE,"E54.0.3")])]})]});
            var Q3;
            Q3=makeQuery(id+"F4.opBoolean","MERGE",EDGE,{"derivedFrom":[makeQuery(id+"F1.opExtrude","SWEPT_EDGE",EDGE,{"disambiguationData":[OSD([sQuery(id+"F0.wireOp",EDGE,"E31.MirrorCS"),sQuery(id+"F0.wireOp",EDGE,"E46.MirrorCS")])]}),makeQuery(id+"F3.opExtrude","SWEPT_EDGE",EDGE,{"disambiguationData":[OSD([sQuery(id+"F2.wireOp",EDGE,"E54.0.11"),sQuery(id+"F2.wireOp",EDGE,"E54.0.12")])]})]});
            var Q4;
            Q4=makeQuery(id+"F4.opBoolean","MERGE",EDGE,{"derivedFrom":[makeQuery(id+"F1.opExtrude","SWEPT_EDGE",EDGE,{"disambiguationData":[OSD([sQuery(id+"F0.wireOp",EDGE,"E36.MirrorCS"),sQuery(id+"F0.wireOp",EDGE,"E50.MirrorCS")])]}),makeQuery(id+"F3.opExtrude","SWEPT_EDGE",EDGE,{"disambiguationData":[OSD([sQuery(id+"F2.wireOp",EDGE,"E54.0.15"),sQuery(id+"F2.wireOp",EDGE,"E54.0.16")])]})]});
            var Q5;
            Q5=makeQuery(id+"F4.opBoolean","MERGE",EDGE,{"derivedFrom":[makeQuery(id+"F1.opExtrude","SWEPT_EDGE",EDGE,{"disambiguationData":[OSD([sQuery(id+"F0.wireOp",EDGE,"E32.MirrorCS"),sQuery(id+"F0.wireOp",EDGE,"E36.MirrorCS")])]}),makeQuery(id+"F3.opExtrude","SWEPT_EDGE",EDGE,{"disambiguationData":[OSD([sQuery(id+"F2.wireOp",EDGE,"E54.0.14"),sQuery(id+"F2.wireOp",EDGE,"E54.0.15")])]})]});
            var Q6;
            Q6=makeQuery(id+"F4.opBoolean","MERGE",EDGE,{"derivedFrom":[makeQuery(id+"F1.opExtrude","SWEPT_EDGE",EDGE,{"disambiguationData":[OSD([sQuery(id+"F0.wireOp",EDGE,"E35.MirrorCS"),sQuery(id+"F0.wireOp",EDGE,"E43.MirrorCS")])]}),makeQuery(id+"F3.opExtrude","SWEPT_EDGE",EDGE,{"disambiguationData":[OSD([sQuery(id+"F2.wireOp",EDGE,"E54.0.4"),sQuery(id+"F2.wireOp",EDGE,"E54.0.5")])]})]});
            var Q7;
            Q7=makeQuery(id+"F4.opBoolean","MERGE",EDGE,{"derivedFrom":[makeQuery(id+"F1.opExtrude","SWEPT_EDGE",EDGE,{"disambiguationData":[OSD([sQuery(id+"F0.wireOp",EDGE,"E34.MirrorCS"),sQuery(id+"F0.wireOp",EDGE,"E50.MirrorCS")])]}),makeQuery(id+"F3.opExtrude","SWEPT_EDGE",EDGE,{"disambiguationData":[OSD([sQuery(id+"F2.wireOp",EDGE,"E54.0.16"),sQuery(id+"F2.wireOp",EDGE,"E54.0.17")])]})]});
            var Q8;
            Q8=makeQuery(id+"F4.opBoolean","MERGE",EDGE,{"derivedFrom":[makeQuery(id+"F1.opExtrude","SWEPT_EDGE",EDGE,{"disambiguationData":[OSD([sQuery(id+"F0.wireOp",EDGE,"E34.MirrorCS"),sQuery(id+"F0.wireOp",EDGE,"E53.MirrorCS")])]}),makeQuery(id+"F3.opExtrude","SWEPT_EDGE",EDGE,{"disambiguationData":[OSD([sQuery(id+"F2.wireOp",EDGE,"E54.0.17"),sQuery(id+"F2.wireOp",EDGE,"E54.0.18")])]})]});
            var Q9;
            Q9=makeQuery(id+"F4.opBoolean","MERGE",EDGE,{"derivedFrom":[makeQuery(id+"F1.opExtrude","SWEPT_EDGE",EDGE,{"disambiguationData":[OSD([sQuery(id+"F0.wireOp",EDGE,"E33.MirrorCS"),sQuery(id+"F0.wireOp",EDGE,"E53.MirrorCS")])]}),makeQuery(id+"F3.opExtrude","SWEPT_EDGE",EDGE,{"disambiguationData":[OSD([sQuery(id+"F2.wireOp",EDGE,"E54.0.18"),sQuery(id+"F2.wireOp",EDGE,"E54.0.19")])]})]});
            var Q10;
            Q10=makeQuery(id+"F4.opBoolean","MERGE",EDGE,{"derivedFrom":[makeQuery(id+"F1.opExtrude","SWEPT_EDGE",EDGE,{"disambiguationData":[OSD([sQuery(id+"F0.wireOp",EDGE,"E33.MirrorCS"),sQuery(id+"F0.wireOp",EDGE,"E41.MirrorCS")])]}),makeQuery(id+"F3.opExtrude","SWEPT_EDGE",EDGE,{"disambiguationData":[OSD([sQuery(id+"F2.wireOp",EDGE,"E54.0.19"),sQuery(id+"F2.wireOp",EDGE,"E54.0.20")])]})]});
            var Q11;
            Q11=makeQuery(id+"F4.opBoolean","MERGE",EDGE,{"derivedFrom":[makeQuery(id+"F1.opExtrude","SWEPT_EDGE",EDGE,{"disambiguationData":[OSD([sQuery(id+"F0.wireOp",EDGE,"E0.top"),sQuery(id+"F0.wireOp",EDGE,"E5")])]}),makeQuery(id+"F3.opExtrude","SWEPT_EDGE",EDGE,{"disambiguationData":[OSD([sQuery(id+"F2.wireOp",EDGE,"E55.0.0"),sQuery(id+"F2.wireOp",EDGE,"E55.0.1")])]})]});
            var Q12;
            Q12=makeQuery(id+"F4.opBoolean","MERGE",EDGE,{"derivedFrom":[makeQuery(id+"F1.opExtrude","SWEPT_EDGE",EDGE,{"disambiguationData":[OSD([sQuery(id+"F0.wireOp",EDGE,"E4"),sQuery(id+"F0.wireOp",EDGE,"E5")])]}),makeQuery(id+"F3.opExtrude","SWEPT_EDGE",EDGE,{"disambiguationData":[OSD([sQuery(id+"F2.wireOp",EDGE,"E55.0.1"),sQuery(id+"F2.wireOp",EDGE,"E55.0.2")])]})]});
            var Q13;
            Q13=makeQuery(id+"F4.opBoolean","MERGE",EDGE,{"derivedFrom":[makeQuery(id+"F1.opExtrude","SWEPT_EDGE",EDGE,{"disambiguationData":[OSD([sQuery(id+"F0.wireOp",EDGE,"E3"),sQuery(id+"F0.wireOp",EDGE,"E4")])]}),makeQuery(id+"F3.opExtrude","SWEPT_EDGE",EDGE,{"disambiguationData":[OSD([sQuery(id+"F2.wireOp",EDGE,"E55.0.2"),sQuery(id+"F2.wireOp",EDGE,"E55.0.3")])]})]});
            var Q14;
            Q14=makeQuery(id+"F4.opBoolean","MERGE",EDGE,{"derivedFrom":[makeQuery(id+"F1.opExtrude","SWEPT_EDGE",EDGE,{"disambiguationData":[OSD([sQuery(id+"F0.wireOp",EDGE,"E3"),sQuery(id+"F0.wireOp",EDGE,"E10.trimOffspring")])]}),makeQuery(id+"F3.opExtrude","SWEPT_EDGE",EDGE,{"disambiguationData":[OSD([sQuery(id+"F2.wireOp",EDGE,"E55.0.3"),sQuery(id+"F2.wireOp",EDGE,"E55.0.4")])]})]});
            var Q15;
            Q15=makeQuery(id+"F4.opBoolean","MERGE",EDGE,{"derivedFrom":[makeQuery(id+"F1.opExtrude","SWEPT_EDGE",EDGE,{"disambiguationData":[OSD([sQuery(id+"F0.wireOp",EDGE,"E9"),sQuery(id+"F0.wireOp",EDGE,"E10.trimOffspring")])]}),makeQuery(id+"F3.opExtrude","SWEPT_EDGE",EDGE,{"disambiguationData":[OSD([sQuery(id+"F2.wireOp",EDGE,"E55.0.4"),sQuery(id+"F2.wireOp",EDGE,"E55.0.5")])]})]});
            var Q16;
            Q16=makeQuery(id+"F4.opBoolean","MERGE",EDGE,{"derivedFrom":[makeQuery(id+"F1.opExtrude","SWEPT_EDGE",EDGE,{"disambiguationData":[OSD([sQuery(id+"F0.wireOp",EDGE,"E8"),sQuery(id+"F0.wireOp",EDGE,"E9")])]}),makeQuery(id+"F3.opExtrude","SWEPT_EDGE",EDGE,{"disambiguationData":[OSD([sQuery(id+"F2.wireOp",EDGE,"E55.0.5"),sQuery(id+"F2.wireOp",EDGE,"E55.0.6")])]})]});
            var Q17;
            Q17=makeQuery(id+"F4.opBoolean","MERGE",EDGE,{"derivedFrom":[makeQuery(id+"F1.opExtrude","SWEPT_EDGE",EDGE,{"disambiguationData":[OSD([sQuery(id+"F0.wireOp",EDGE,"E15"),sQuery(id+"F0.wireOp",EDGE,"E16.trimOffspring")])]}),makeQuery(id+"F3.opExtrude","SWEPT_EDGE",EDGE,{"disambiguationData":[OSD([sQuery(id+"F2.wireOp",EDGE,"E55.0.8"),sQuery(id+"F2.wireOp",EDGE,"E55.0.9")])]})]});
            var Q18;
            Q18=makeQuery(id+"F4.opBoolean","MERGE",EDGE,{"derivedFrom":[makeQuery(id+"F1.opExtrude","SWEPT_EDGE",EDGE,{"disambiguationData":[OSD([sQuery(id+"F0.wireOp",EDGE,"E12"),sQuery(id+"F0.wireOp",EDGE,"E22")])]}),makeQuery(id+"F3.opExtrude","SWEPT_EDGE",EDGE,{"disambiguationData":[OSD([sQuery(id+"F2.wireOp",EDGE,"E55.0.15"),sQuery(id+"F2.wireOp",EDGE,"E55.0.16")])]})]});
            var Q19;
            Q19=makeQuery(id+"F4.opBoolean","MERGE",EDGE,{"derivedFrom":[makeQuery(id+"F1.opExtrude","SWEPT_EDGE",EDGE,{"disambiguationData":[OSD([sQuery(id+"F0.wireOp",EDGE,"E0.left"),sQuery(id+"F0.wireOp",EDGE,"E13")])]}),makeQuery(id+"F3.opExtrude","SWEPT_EDGE",EDGE,{"disambiguationData":[OSD([sQuery(id+"F2.wireOp",EDGE,"E55.0.17"),sQuery(id+"F2.wireOp",EDGE,"E55.0.18")])]})]});
            var Q20;
            Q20=makeQuery(id+"F4.opBoolean","MERGE",EDGE,{"derivedFrom":[makeQuery(id+"F1.opExtrude","SWEPT_EDGE",EDGE,{"disambiguationData":[OSD([sQuery(id+"F0.wireOp",EDGE,"E0.left"),sQuery(id+"F0.wireOp",EDGE,"E1")])]}),makeQuery(id+"F3.opExtrude","SWEPT_EDGE",EDGE,{"disambiguationData":[OSD([sQuery(id+"F2.wireOp",EDGE,"E55.0.18"),sQuery(id+"F2.wireOp",EDGE,"E55.0.19")])]})]});
            var Q21;
            Q21=makeQuery(id+"F4.opBoolean","MERGE",EDGE,{"derivedFrom":[makeQuery(id+"F1.opExtrude","SWEPT_EDGE",EDGE,{"disambiguationData":[OSD([sQuery(id+"F0.wireOp",EDGE,"E0.bottom"),sQuery(id+"F0.wireOp",EDGE,"E1")])]}),makeQuery(id+"F3.opExtrude","SWEPT_EDGE",EDGE,{"disambiguationData":[OSD([sQuery(id+"F2.wireOp",EDGE,"E55.0.19"),sQuery(id+"F2.wireOp",EDGE,"E55.0.20")])]})]});
            fillet(context, id + "F8", {"entities" : qUnion([Q0, Q1, Q2, Q3, Q4, Q5, Q6, Q7, Q8, Q9, Q10, Q11, Q12, Q13, Q14, Q15, Q16, Q17, Q18, Q19, Q20, Q21]), "radius" : 0.5 * mm, "tangentPropagation" : true, "allowEdgeOverflow" : false});
        }
    });
